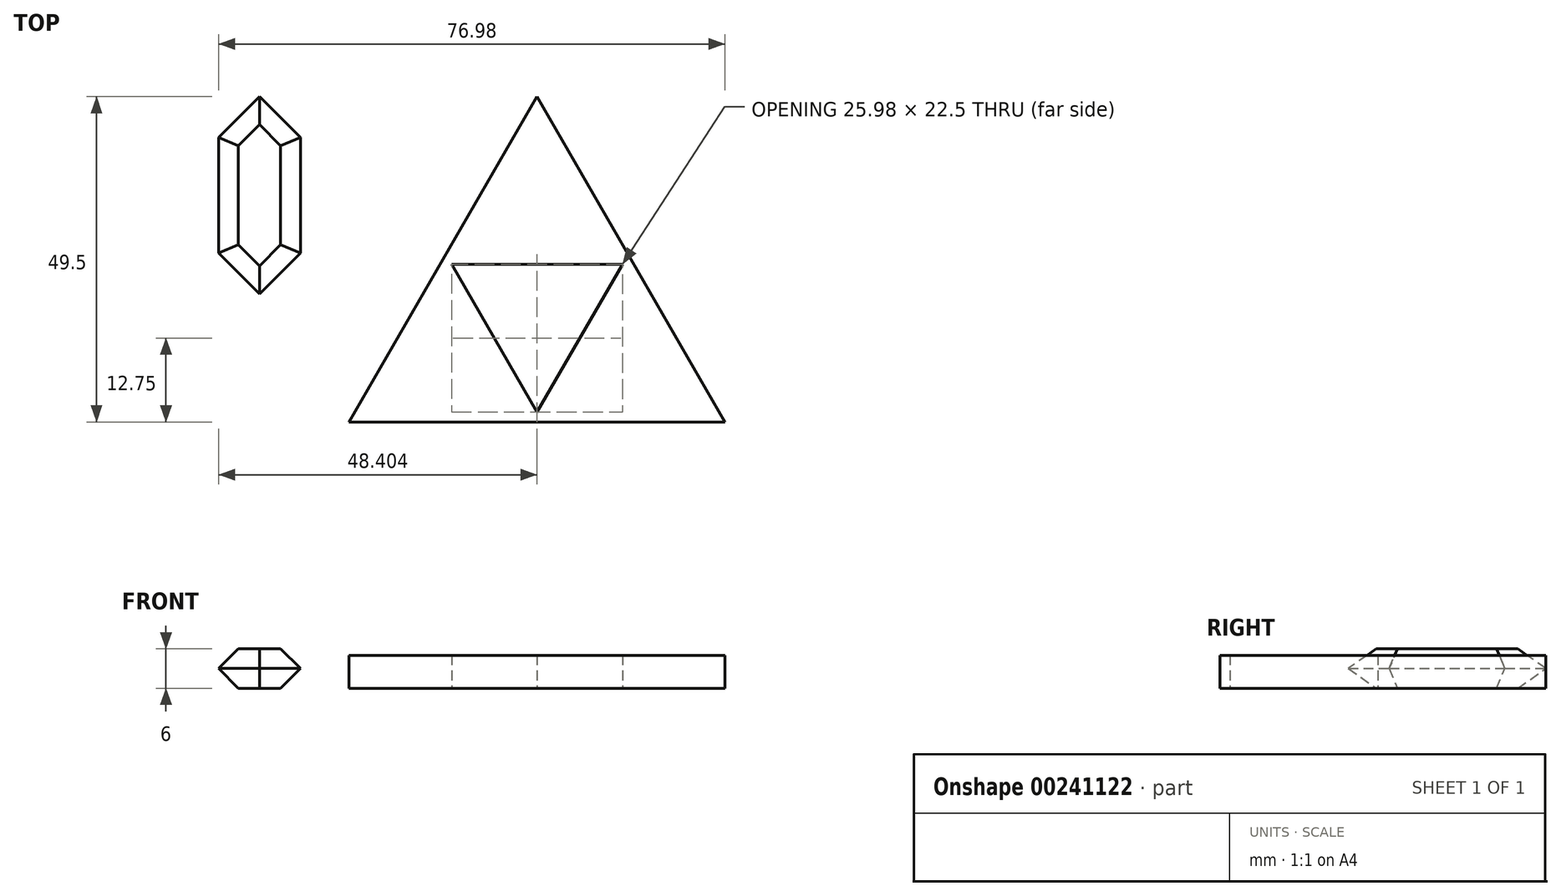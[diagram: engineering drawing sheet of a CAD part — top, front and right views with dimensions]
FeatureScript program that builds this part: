
annotation { "Feature Type Name" : "Feature", "Feature Type Description" : "" }
export const myFeature = defineFeature(function(context is Context, id is Id, definition is map)
    precondition{}
    {
        {
            var Q0;
            Q0=qCreatedBy(makeId("Top.planeOp"),FACE);
            var sketch = newSketch(context, id + "F0", { "sketchPlane" : qUnion([Q0])});
            skLineSegment(sketch, "E0", {"start": v(-6.21, 0) * mm, "end": v(-6.21, 8.79) * mm});
            skLineSegment(sketch, "E1", {"start": v(-6.21, 8.79) * mm, "end": v(0, 15) * mm});
            skLineSegment(sketch, "E2.MirrorCS", {"start": v(6.21, 8.79) * mm, "end": v(0, 15) * mm});
            skLineSegment(sketch, "E3.MirrorCS", {"start": v(6.21, 0) * mm, "end": v(6.21, 8.79) * mm});
            skLineSegment(sketch, "E4.MirrorCS", {"start": v(-6.21, 0) * mm, "end": v(-6.21, -8.79) * mm});
            skLineSegment(sketch, "E5.MirrorCS", {"start": v(-6.21, -8.79) * mm, "end": v(0, -15) * mm});
            skLineSegment(sketch, "E6.MirrorCS", {"start": v(6.21, -8.79) * mm, "end": v(0, -15) * mm});
            skLineSegment(sketch, "E7.MirrorCS", {"start": v(6.21, 0) * mm, "end": v(6.21, -8.79) * mm});
            skSolve(sketch);
        }
        {
            var Q0;
            Q0 = qSketchRegion(id + "F0", true);
            extrude(context, id + "F1", {"entities" : qUnion([Q0]), "depth" : 6 * mm});
        }
        {
            var Q0;
            Q0=makeQuery(id+"F1.opExtrude","CAP_EDGE",EDGE,{"disambiguationData":[OSD([sQuery(id+"F0.wireOp",EDGE,"E1")])],"isStart":false});
            var Q1;
            Q1=makeQuery(id+"F1.opExtrude","CAP_EDGE",EDGE,{"disambiguationData":[OSD([sQuery(id+"F0.wireOp",EDGE,"E2.MirrorCS")])],"isStart":false});
            var Q2;
            Q2=makeQuery(id+"F1.opExtrude","CAP_EDGE",EDGE,{"disambiguationData":[OSD([sQuery(id+"F0.wireOp",EDGE,"E3.MirrorCS"),sQuery(id+"F0.wireOp",EDGE,"E7.MirrorCS")])],"isStart":false});
            var Q3;
            Q3=makeQuery(id+"F1.opExtrude","CAP_EDGE",EDGE,{"disambiguationData":[OSD([sQuery(id+"F0.wireOp",EDGE,"E0"),sQuery(id+"F0.wireOp",EDGE,"E4.MirrorCS")])],"isStart":false});
            var Q4;
            Q4=makeQuery(id+"F1.opExtrude","CAP_EDGE",EDGE,{"disambiguationData":[OSD([sQuery(id+"F0.wireOp",EDGE,"E5.MirrorCS")])],"isStart":false});
            var Q5;
            Q5=makeQuery(id+"F1.opExtrude","CAP_EDGE",EDGE,{"disambiguationData":[OSD([sQuery(id+"F0.wireOp",EDGE,"E6.MirrorCS")])],"isStart":false});
            var Q6;
            Q6=makeQuery(id+"F1.opExtrude","CAP_EDGE",EDGE,{"disambiguationData":[OSD([sQuery(id+"F0.wireOp",EDGE,"E1")])],"isStart":true});
            var Q7;
            Q7=makeQuery(id+"F1.opExtrude","CAP_EDGE",EDGE,{"disambiguationData":[OSD([sQuery(id+"F0.wireOp",EDGE,"E0"),sQuery(id+"F0.wireOp",EDGE,"E4.MirrorCS")])],"isStart":true});
            var Q8;
            Q8=makeQuery(id+"F1.opExtrude","CAP_EDGE",EDGE,{"disambiguationData":[OSD([sQuery(id+"F0.wireOp",EDGE,"E5.MirrorCS")])],"isStart":true});
            var Q9;
            Q9=makeQuery(id+"F1.opExtrude","CAP_EDGE",EDGE,{"disambiguationData":[OSD([sQuery(id+"F0.wireOp",EDGE,"E6.MirrorCS")])],"isStart":true});
            var Q10;
            Q10=makeQuery(id+"F1.opExtrude","CAP_EDGE",EDGE,{"disambiguationData":[OSD([sQuery(id+"F0.wireOp",EDGE,"E3.MirrorCS"),sQuery(id+"F0.wireOp",EDGE,"E7.MirrorCS")])],"isStart":true});
            var Q11;
            Q11=makeQuery(id+"F1.opExtrude","CAP_EDGE",EDGE,{"disambiguationData":[OSD([sQuery(id+"F0.wireOp",EDGE,"E2.MirrorCS")])],"isStart":true});
            chamfer(context, id + "F2", {"entities" : qUnion([Q0, Q1, Q2, Q3, Q4, Q5, Q6, Q7, Q8, Q9, Q10, Q11]), "width" : 3 * mm, "tangentPropagation" : true});
        }
        {
            var Q0;
            Q0=qCreatedBy(makeId("Top.planeOp"),FACE);
            var sketch = newSketch(context, id + "F3", { "sketchPlane" : qUnion([Q0])});
            skLineSegment(sketch, "E8", {"start": v(42.2, -10.5) * mm, "end": v(55.18, -10.5) * mm});
            skLineSegment(sketch, "E9", {"start": v(55.18, -10.5) * mm, "end": v(42.2, 12) * mm, "construction": true});
            skLineSegment(sketch, "E10", {"start": v(55.18, -10.5) * mm, "end": v(42.2, -33) * mm});
            skLineSegment(sketch, "E11", {"start": v(42.2, -33) * mm, "end": v(68.17, -33) * mm, "construction": true});
            skLineSegment(sketch, "E12", {"start": v(68.17, -33) * mm, "end": v(55.18, -10.5) * mm, "construction": true});
            skLineSegment(sketch, "E13", {"start": v(42.2, 12) * mm, "end": v(42.2, -10.5) * mm, "construction": true});
            skLineSegment(sketch, "E14", {"start": v(42.2, -10.5) * mm, "end": v(42.2, -33) * mm, "construction": true});
            skLineSegment(sketch, "E15.MirrorCS", {"start": v(29.2, -10.5) * mm, "end": v(42.2, 12) * mm, "construction": true});
            skLineSegment(sketch, "E16.MirrorCS", {"start": v(42.2, -10.5) * mm, "end": v(29.2, -10.5) * mm});
            skLineSegment(sketch, "E17.MirrorCS", {"start": v(29.2, -10.5) * mm, "end": v(42.2, -33) * mm});
            skLineSegment(sketch, "E18.MirrorCS", {"start": v(42.2, -33) * mm, "end": v(16.21, -33) * mm, "construction": true});
            skLineSegment(sketch, "E19.MirrorCS", {"start": v(16.21, -33) * mm, "end": v(29.2, -10.5) * mm, "construction": true});
            skLineSegment(sketch, "E20.0", {"start": v(13.62, -34.5) * mm, "end": v(28.3, -9.06) * mm});
            skLineSegment(sketch, "E20.1", {"start": v(58.19, -12.7) * mm, "end": v(42.2, 15) * mm});
            skLineSegment(sketch, "E20.2", {"start": v(70.77, -34.5) * mm, "end": v(58.19, -12.7) * mm});
            skLineSegment(sketch, "E20.3", {"start": v(28.3, -9.06) * mm, "end": v(42.2, 15) * mm});
            skLineSegment(sketch, "E20.4", {"start": v(28.84, -34.5) * mm, "end": v(70.77, -34.5) * mm});
            skLineSegment(sketch, "E20.5", {"start": v(28.84, -34.5) * mm, "end": v(13.62, -34.5) * mm});
            skSolve(sketch);
        }
        {
            var Q0;
            Q0 = qSketchRegion(id + "F3", true);
            extrude(context, id + "F4", {"entities" : qUnion([Q0]), "depth" : 5 * mm});
        }
    });
